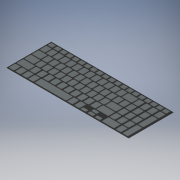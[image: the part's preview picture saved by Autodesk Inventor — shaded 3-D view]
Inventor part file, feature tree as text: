
AUTODESK INVENTOR PART (.ipt)
format: ipt  version: 2025 (Build 290162000, 162)  size: 1,055,744 bytes
history: native  units: in
note: dims shown in document units (in); Inventor stores cm internally (conversion verified against a paired STEP export)
features: extrude x22, sketch x19, pattern_linear x10
ambient origin geometry x8: Origin, YZ Plane, XZ Plane, XY Plane, X Axis, Y Axis, Z Axis, Center Point
bodies: Solid1 (feature_tree)
feature tree (51):
  extrude  "KEYBOARD BASE"  Depth=4.3303in
  extrude  "ESCAPE BUTTON"  Depth=0.3937in
  pattern_linear  "1ST ROW"  Count1=20 Spacing1=0.5807in
  extrude  "2ND ROW"  Depth=0.6772in
  pattern_linear  "2ND ROW PATTERN"  Count1=13 Spacing1=0.6102in
  extrude  "BACKSPACE BUTTON"  Depth=0.6772in
  extrude  "NUM LOCK BUTTON"  Depth=0.0118in TaperAngle=0.0deg
  pattern_linear  "NUMERIC KEYPAD"  Count1=3 Spacing1=0.6693in
  extrude  "SUBTRACT BUTTON"  Depth=0.6772in
  extrude  "ADD BUTTON"  Depth=0.5315in
  pattern_linear  "ENTER BUTTON"  Count1=2 Spacing1=1.4961in
  extrude  "0 BUTTON"  Depth=0.6772in
  extrude  "DOT BUTTON"  Depth=0.0118in TaperAngle=0.0deg
  extrude  "TAB BUTTON"  Depth=0.0118in TaperAngle=0.0deg
  extrude  "Q BUTTON"  Depth=0.9449in
  pattern_linear  "QWERTY"  Count1=11 Spacing1=0.6201in
  extrude  "CAPS LOCK"  Depth=1.063in
  extrude  "A BUTTON"  Depth=0.6772in
  pattern_linear  "ASDFGH"  Spacing1=0.0118in  [1 undecoded]
  extrude  "ENTER BUTTON 1"  Depth=1.1811in
  extrude  "LEFT SHIFT"  Depth=0.6772in
  extrude  "Z BUTTON"  Depth=0.0118in TaperAngle=0.0deg
  pattern_linear  "ZXCVBN"  Spacing1=0.0118in  [1 undecoded]
  extrude  "SPACE BAR"  Depth=3.937in
  extrude  "RIGHT SHIFT"  Depth=0.6772in
  extrude  "CTRL BUTTON"  Depth=3.0512in
  pattern_linear  "FN/WIN/ALT"  Spacing1=0.0118in  [1 undecoded]
  extrude  "ALT BUTTON"  Depth=0.0118in TaperAngle=0.0deg
  pattern_linear  "CTRL RIGHT"  Spacing1=0.0118in  [1 undecoded]
  extrude  "LEFT ARROW KEY"  Depth=1.5748in
  pattern_linear  "ARROW KEYS"  Spacing1=0.0118in  [1 undecoded]
  extrude  "UP ARROW KEY"  Depth=0.7874in
  sketch  "Sketch1"  dims[d2=11.8102in d3=4.3303in]
  sketch  "Sketch2"  dims[d4=0.0004in d5=0.0in d9=0.3937in]
  sketch  "Sketch3"  dims[d10=0.4724in]
  sketch  "Sketch6"  dims[d11=0.0118in d12=0.0in d13=7.874in d15=0.5807in]
  sketch  "Sketch7"  dims[d19=0.5315in d20=0.6772in]
  sketch  "Sketch9"  dims[d21=0.0118in d22=0.0in d23=5.1181in d25=0.6102in]
  sketch  "Sketch10"  dims[d31=0.9843in d32=0.6772in]
  sketch  "Sketch11"  dims[d33=0.0118in d34=0.0in d38=0.0118in d39=0.0in d40=1.1811in d42=0.6693in d43=1.5748in d45=0.748in]
  sketch  "Sketch12"  dims[d52=0.5315in d53=0.6772in]
  sketch  "Sketch13"  dims[d54=0.0118in d55=0.0in d56=0.5315in]
  sketch  "Sketch14"  dims[d57=1.4252in]
  sketch  "Sketch15"  dims[d58=0.0118in d59=0.0in d60=0.7874in d62=1.4961in]
  sketch  "Sketch16"  dims[d63=1.2008in d64=0.6772in]
  sketch  "Sketch17"  dims[d65=0.0118in d66=0.0in d69=0.0118in d70=0.0in]
  sketch  "Sketch18"  dims[d73=0.0118in d74=0.0in d77=0.0118in d78=0.0in]
  sketch  "Sketch19"  dims[d79=5.1181in d81=0.6181in d84=0.9449in]
  sketch  "Sketch20"  dims[d85=0.6772in]
  sketch  "Sketch21"  dims[d86=0.0118in d87=0.0in]
  sketch  "Sketch22"  dims[d90=0.0118in d91=0.0in d92=4.3307in d94=0.6201in d95=1.063in d96=0.6772in d97=0.0118in d98=0.0in d101=1.1811in d102=0.6772in d103=0.0118in d104=0.0in d107=0.0118in d108=0.0in d109=3.937in d111=0.6496in d112=0.6772in d113=3.0512in d114=0.0118in d115=0.0in d118=0.0118in d119=0.0in d122=0.0118in d123=0.0in d124=1.5748in d126=0.6299in d129=0.0118in d130=0.0in d131=0.7874in d133=0.6693in d136=0.5315in d137=0.2953in d138=0.0118in d139=0.0in d143=1.1811in d145=0.689in d148=0.0118in d149=0.0in d150=0.0394in d151=0.0787in d152=0.0787in d153=0.0787in d154=0.0787in d155=0.0787in d156=0.0787in d157=0.0787in d158=0.0787in d159=0.0787in d160=0.0787in d161=0.0787in d162=0.0787in d163=0.0787in d164=0.0787in d165=0.0787in d166=0.0787in d167=0.0787in d168=0.0787in d169=0.0787in d170=0.0787in]
note: 5 required parameter values undecoded (feature->parameter linkage not recoverable at this tier; creation-order binding heuristic only, values carry confidence <= 0.55)
